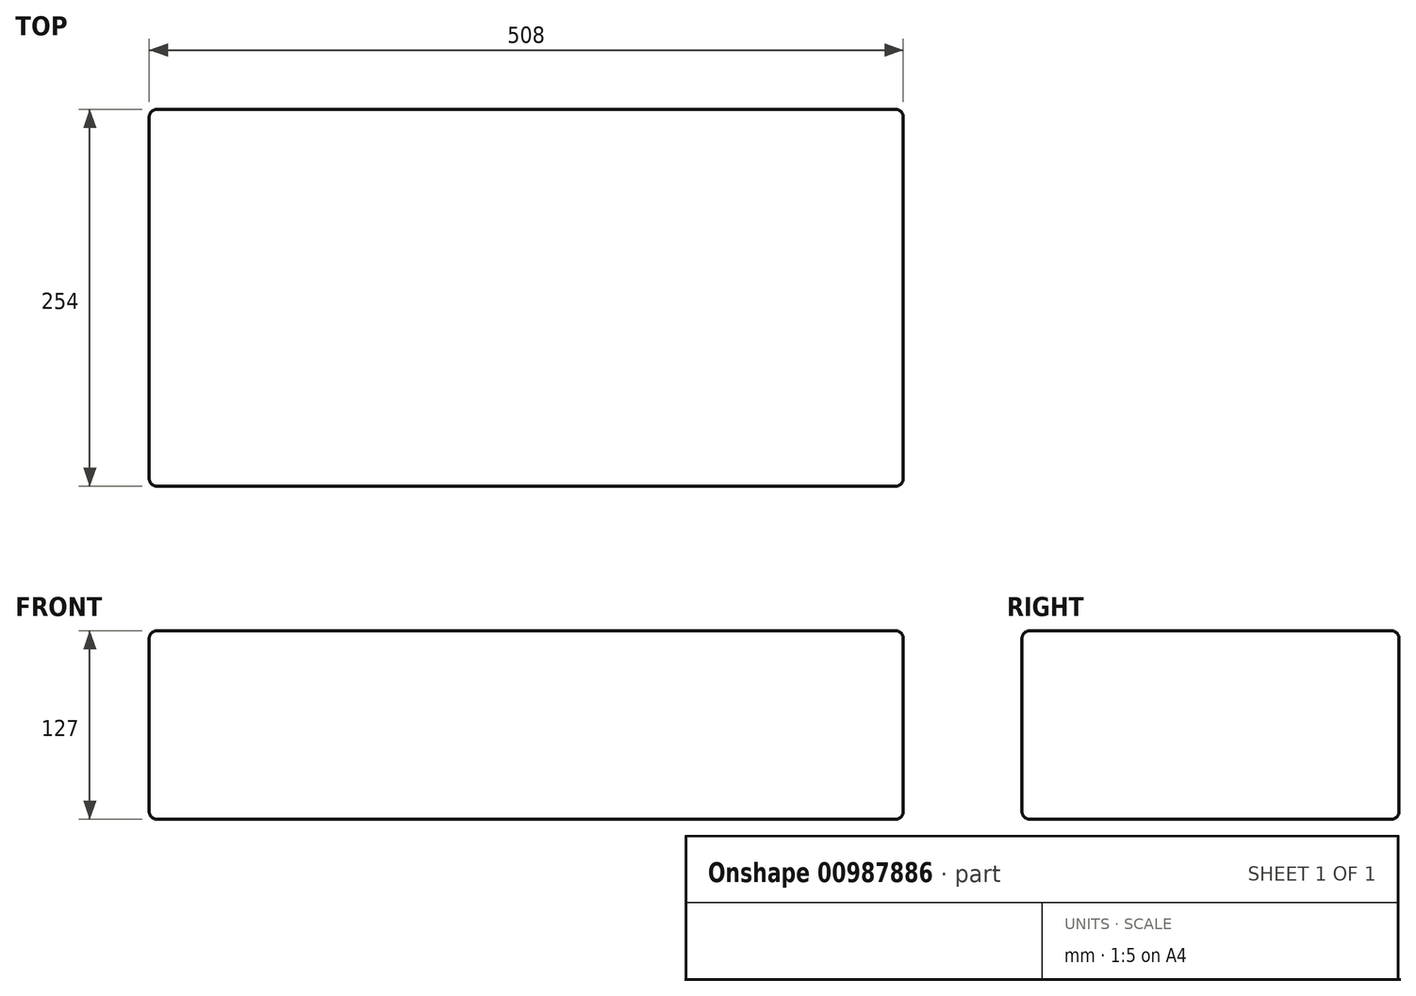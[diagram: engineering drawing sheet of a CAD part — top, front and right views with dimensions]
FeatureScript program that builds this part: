
annotation { "Feature Type Name" : "Feature", "Feature Type Description" : "" }
export const myFeature = defineFeature(function(context is Context, id is Id, definition is map)
    precondition{}
    {
        {
            var Q0;
            Q0=qCreatedBy(makeId("Top.planeOp"),FACE);
            var sketch = newSketch(context, id + "F0", { "sketchPlane" : qUnion([Q0])});
            skLineSegment(sketch, "E0.bottom", {"start": v(-433.24, 217.22) * mm, "end": v(74.76, 217.22) * mm});
            skLineSegment(sketch, "E0.top", {"start": v(-433.24, -36.78) * mm, "end": v(74.76, -36.78) * mm});
            skLineSegment(sketch, "E0.left", {"start": v(-433.24, 217.22) * mm, "end": v(-433.24, -36.78) * mm});
            skLineSegment(sketch, "E0.right", {"start": v(74.76, 217.22) * mm, "end": v(74.76, -36.78) * mm});
            skSolve(sketch);
        }
        {
            var Q0;
            Q0=makeQuery(id+"F0.imprint","IMPRINT",FACE,{"disambiguationData":[TD([[makeQuery(id+"F0.imprint","IMPRINT",EDGE,{"derivedFrom":sQuery(id+"F0.wireOp",EDGE,"E0.bottom")}),-1.0]])]});
            extrude(context, id + "F1", {"entities" : qUnion([Q0]), "depth" : 127 * mm, "offsetDistance" : 25.4 * mm});
        }
        {
            var Q0;
            Q0=makeQuery(id+"F1.opExtrude","SWEPT_EDGE",EDGE,{"disambiguationData":[OSD([sQuery(id+"F0.wireOp",EDGE,"E0.top"),sQuery(id+"F0.wireOp",EDGE,"E0.left")])]});
            var Q1;
            Q1=makeQuery(id+"F1.opExtrude","CAP_EDGE",EDGE,{"disambiguationData":[OSD([sQuery(id+"F0.wireOp",EDGE,"E0.top")])],"isStart":false});
            var Q2;
            Q2=makeQuery(id+"F1.opExtrude","CAP_EDGE",EDGE,{"disambiguationData":[OSD([sQuery(id+"F0.wireOp",EDGE,"E0.left")])],"isStart":false});
            var Q3;
            Q3=makeQuery(id+"F1.opExtrude","SWEPT_EDGE",EDGE,{"disambiguationData":[OSD([sQuery(id+"F0.wireOp",EDGE,"E0.bottom"),sQuery(id+"F0.wireOp",EDGE,"E0.left")])]});
            var Q4;
            Q4=makeQuery(id+"F1.opExtrude","CAP_EDGE",EDGE,{"disambiguationData":[OSD([sQuery(id+"F0.wireOp",EDGE,"E0.bottom")])],"isStart":false});
            var Q5;
            Q5=makeQuery(id+"F1.opExtrude","CAP_EDGE",EDGE,{"disambiguationData":[OSD([sQuery(id+"F0.wireOp",EDGE,"E0.left")])],"isStart":true});
            var Q6;
            Q6=makeQuery(id+"F1.opExtrude","CAP_EDGE",EDGE,{"disambiguationData":[OSD([sQuery(id+"F0.wireOp",EDGE,"E0.bottom")])],"isStart":true});
            var Q7;
            Q7=makeQuery(id+"F1.opExtrude","CAP_EDGE",EDGE,{"disambiguationData":[OSD([sQuery(id+"F0.wireOp",EDGE,"E0.top")])],"isStart":true});
            var Q8;
            Q8=makeQuery(id+"F1.opExtrude","CAP_EDGE",EDGE,{"disambiguationData":[OSD([sQuery(id+"F0.wireOp",EDGE,"E0.right")])],"isStart":true});
            var Q9;
            Q9=makeQuery(id+"F1.opExtrude","SWEPT_EDGE",EDGE,{"disambiguationData":[OSD([sQuery(id+"F0.wireOp",EDGE,"E0.top"),sQuery(id+"F0.wireOp",EDGE,"E0.right")])]});
            var Q10;
            Q10=makeQuery(id+"F1.opExtrude","CAP_EDGE",EDGE,{"disambiguationData":[OSD([sQuery(id+"F0.wireOp",EDGE,"E0.right")])],"isStart":false});
            var Q11;
            Q11=makeQuery(id+"F1.opExtrude","SWEPT_EDGE",EDGE,{"disambiguationData":[OSD([sQuery(id+"F0.wireOp",EDGE,"E0.bottom"),sQuery(id+"F0.wireOp",EDGE,"E0.right")])]});
            fillet(context, id + "F2", {"entities" : qUnion([Q0, Q1, Q2, Q3, Q4, Q5, Q6, Q7, Q8, Q9, Q10, Q11]), "radius" : 5.08 * mm, "tangentPropagation" : true, "allowEdgeOverflow" : false});
        }
    });
